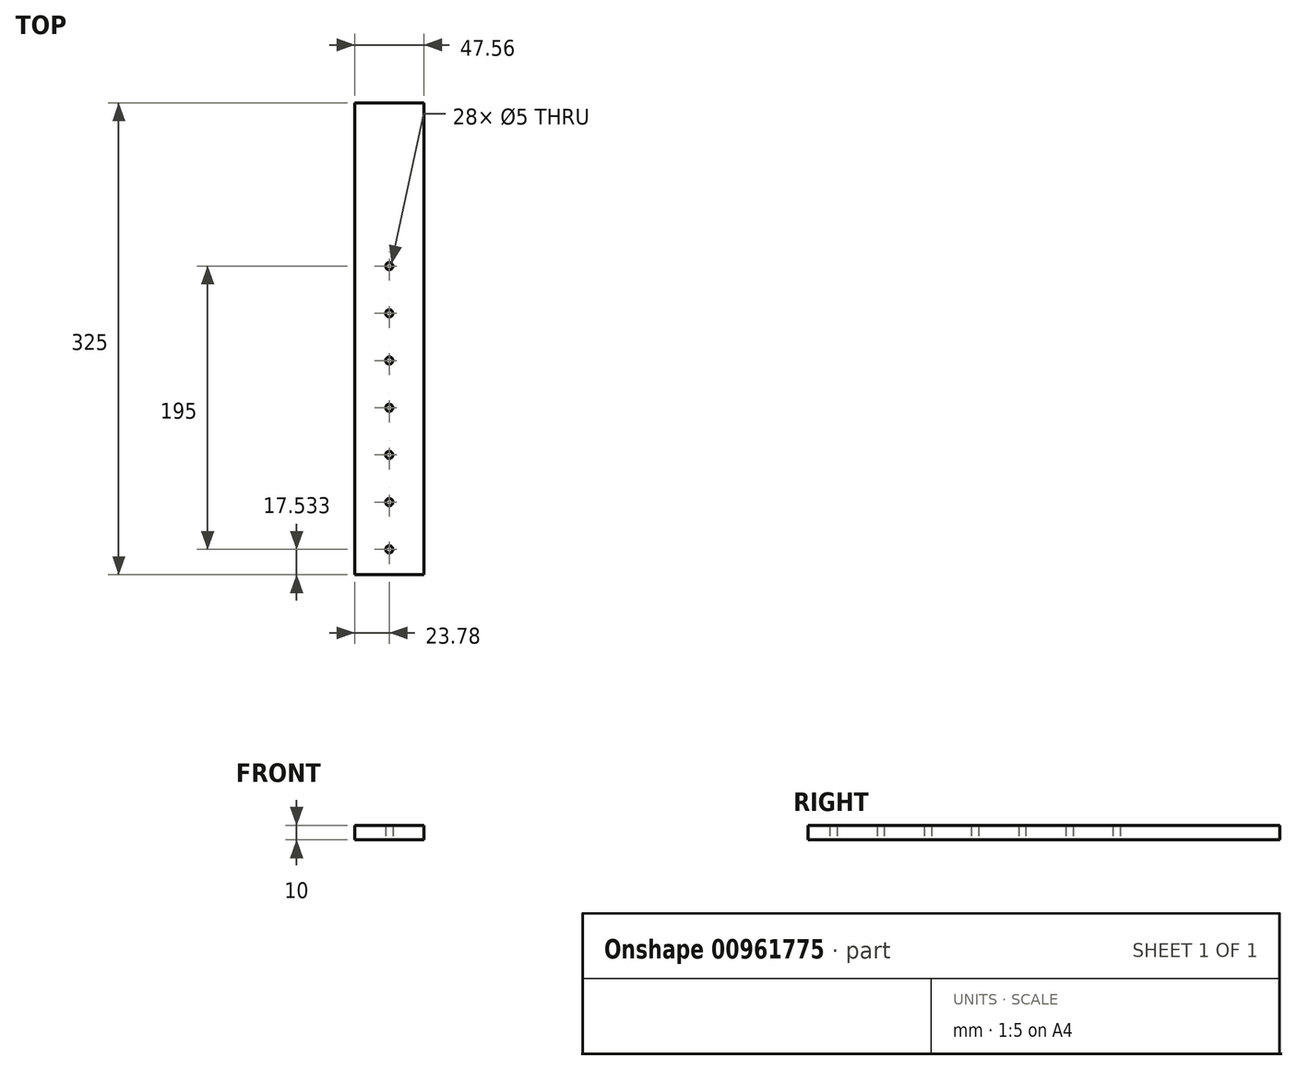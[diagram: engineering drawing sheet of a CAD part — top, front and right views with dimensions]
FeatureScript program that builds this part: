
annotation { "Feature Type Name" : "Feature", "Feature Type Description" : "" }
export const myFeature = defineFeature(function(context is Context, id is Id, definition is map)
    precondition{}
    {
        {
            var Q0;
            Q0=qCreatedBy(makeId("Top.planeOp"),FACE);
            var sketch = newSketch(context, id + "F0", { "sketchPlane" : qUnion([Q0])});
            skLineSegment(sketch, "E0.bottom", {"start": v(23.78, -162.5) * mm, "end": v(-23.78, -162.5) * mm});
            skLineSegment(sketch, "E0.top", {"start": v(23.78, 162.5) * mm, "end": v(-23.78, 162.5) * mm});
            skLineSegment(sketch, "E0.left", {"start": v(23.78, -162.5) * mm, "end": v(23.78, 162.5) * mm});
            skLineSegment(sketch, "E0.right", {"start": v(-23.78, -162.5) * mm, "end": v(-23.78, 162.5) * mm});
            skPoint(sketch, "E0.middle", {"position": v(0, 0) * mm});
            skCircle(sketch, "E1", {"center": v(0, 50.03) * mm, "radius": 2.5 * mm});
            skCircle(sketch, "E2.0.1.0", {"center": v(0, 17.53) * mm, "radius": 2.5 * mm});
            skCircle(sketch, "E2.0.2.0", {"center": v(0, -14.97) * mm, "radius": 2.5 * mm});
            skCircle(sketch, "E2.0.3.0", {"center": v(0, -47.47) * mm, "radius": 2.5 * mm});
            skCircle(sketch, "E2.0.4.0", {"center": v(0, -79.97) * mm, "radius": 2.5 * mm});
            skLineSegment(sketch, "E2.direction1", {"start": v(0, 50.03) * mm, "end": v(25, 50.03) * mm, "construction": true});
            skLineSegment(sketch, "E2.direction2", {"start": v(0, 50.03) * mm, "end": v(0, 17.53) * mm, "construction": true});
            skCircle(sketch, "E3.0.0.5", {"center": v(0, -112.47) * mm, "radius": 2.5 * mm});
            skCircle(sketch, "E3.0.0.6", {"center": v(0, -144.97) * mm, "radius": 2.5 * mm});
            skCircle(sketch, "E3.0.0.7", {"center": v(0, -177.47) * mm, "radius": 2.5 * mm});
            skCircle(sketch, "E3.0.0.8", {"center": v(0, -209.97) * mm, "radius": 2.5 * mm});
            skCircle(sketch, "E3.0.0.9", {"center": v(0, -242.47) * mm, "radius": 2.5 * mm});
            skSolve(sketch);
        }
        {
            var Q0;
            Q0=makeQuery(id+"F0.imprint","IMPRINT",FACE,{"disambiguationData":[TD([[makeQuery(id+"F0.imprint","IMPRINT",EDGE,{"derivedFrom":sQuery(id+"F0.wireOp",EDGE,"E0.bottom")}),-1.0]])]});
            extrude(context, id + "F1", {"entities" : qUnion([Q0]), "depth" : 10 * mm, "offsetDistance" : 25 * mm});
        }
    });
